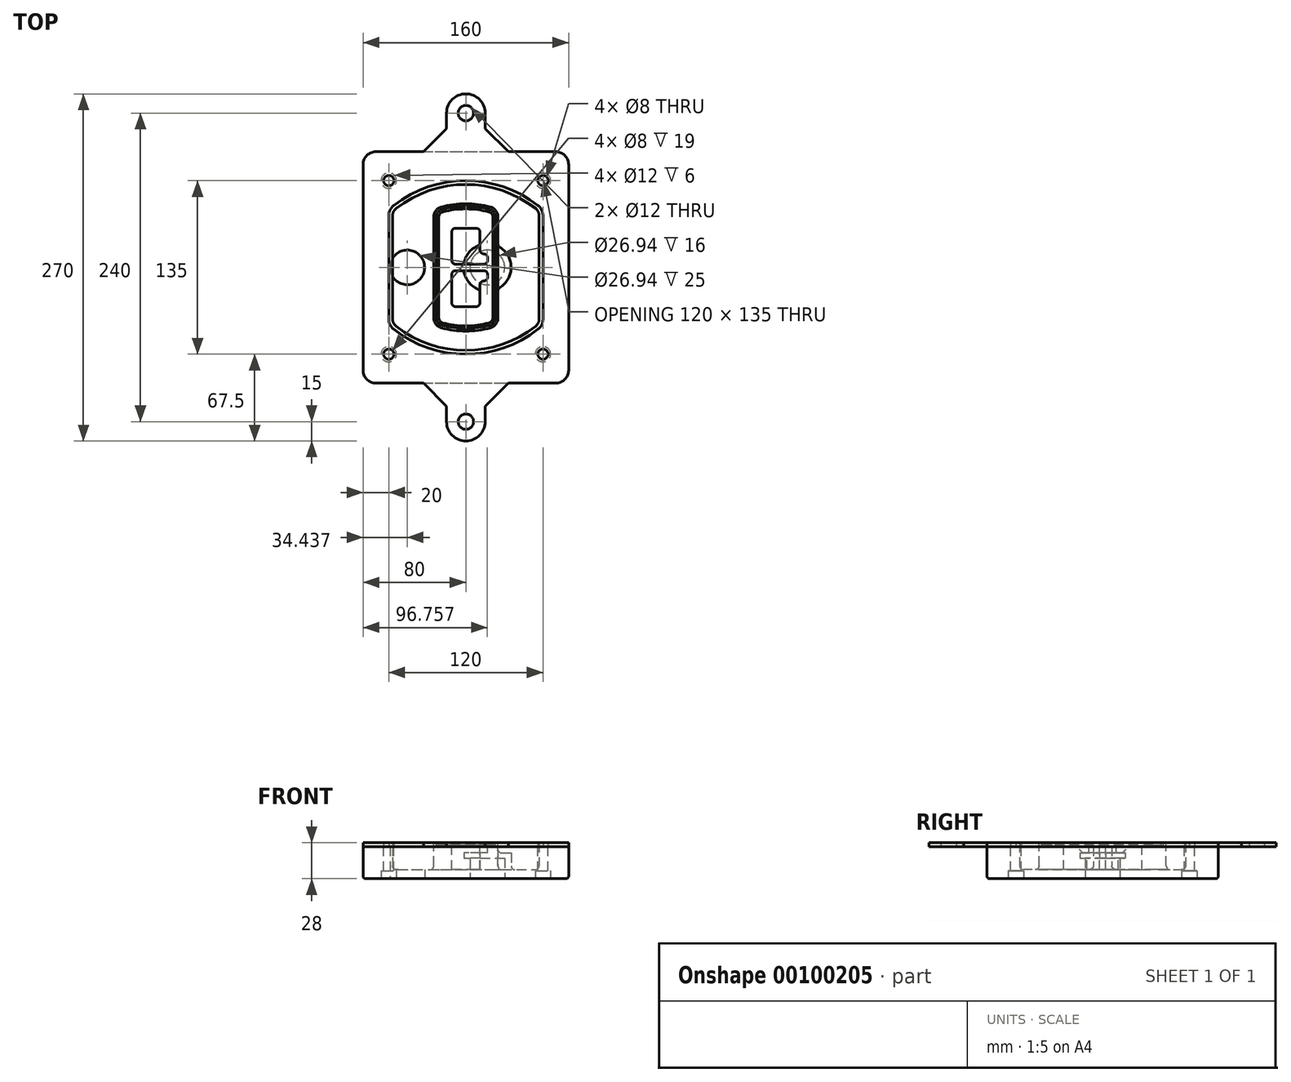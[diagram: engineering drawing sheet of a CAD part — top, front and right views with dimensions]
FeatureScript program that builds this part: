
annotation { "Feature Type Name" : "Feature", "Feature Type Description" : "" }
export const myFeature = defineFeature(function(context is Context, id is Id, definition is map)
    precondition{}
    {
        {
            var Q0;
            Q0=qCreatedBy(makeId("Top.planeOp"),FACE);
            var sketch = newSketch(context, id + "F0", { "sketchPlane" : qUnion([Q0])});
            skPoint(sketch, "E0.rect.middle", {"position": v(0, 0) * mm});
            skLineSegment(sketch, "E1.bottom", {"start": v(-70, -90) * mm, "end": v(70, -90) * mm});
            skLineSegment(sketch, "E1.top", {"start": v(-70, 90) * mm, "end": v(70, 90) * mm});
            skLineSegment(sketch, "E1.left", {"start": v(-80, -80) * mm, "end": v(-80, 80) * mm});
            skLineSegment(sketch, "E1.right", {"start": v(80, -80) * mm, "end": v(80, 80) * mm});
            skLineSegment(sketch, "E2", {"start": v(-80, 90) * mm, "end": v(80, -90) * mm, "construction": true});
            skLineSegment(sketch, "E3", {"start": v(80, 90) * mm, "end": v(-80, -90) * mm, "construction": true});
            skCircle(sketch, "E4", {"center": v(-60, 67.5) * mm, "radius": 4 * mm});
            skCircle(sketch, "E5", {"center": v(60, 67.5) * mm, "radius": 4 * mm});
            skCircle(sketch, "E6", {"center": v(60, -67.5) * mm, "radius": 4 * mm});
            skCircle(sketch, "E7", {"center": v(-60, -67.5) * mm, "radius": 4 * mm});
            skLineSegment(sketch, "E8", {"start": v(-60, 67.5) * mm, "end": v(60, 67.5) * mm, "construction": true});
            skLineSegment(sketch, "E9", {"start": v(60, 67.5) * mm, "end": v(60, -67.5) * mm, "construction": true});
            skLineSegment(sketch, "E10", {"start": v(60, -67.5) * mm, "end": v(-60, -67.5) * mm, "construction": true});
            skLineSegment(sketch, "E11", {"start": v(-60, -67.5) * mm, "end": v(-60, 67.5) * mm, "construction": true});
            skLineSegment(sketch, "E12", {"start": v(-60, 40.3) * mm, "end": v(-60, -40.3) * mm});
            skLineSegment(sketch, "E13", {"start": v(60, 40.3) * mm, "end": v(60, -40.3) * mm});
            skArc(sketch, "E14", {"start": v(56.15, 48.18) * mm, "mid": v(0, 67.5) * mm, "end": v(-56.15, 48.18) * mm});
            skArc(sketch, "E15", {"start": v(-56.15, -48.18) * mm, "mid": v(0, -67.5) * mm, "end": v(56.15, -48.18) * mm});
            skLineSegment(sketch, "E16", {"start": v(-60, 0) * mm, "end": v(60, 0) * mm, "construction": true});
            skPoint(sketch, "E17.visualSharp", {"position": v(-60, -45) * mm});
            skArc(sketch, "E17.filletArc", {"start": v(-60, -40.3) * mm, "mid": v(-58.99, -44.68) * mm, "end": v(-56.15, -48.18) * mm});
            skPoint(sketch, "E18.visualSharp", {"position": v(-60, 45) * mm});
            skArc(sketch, "E18.filletArc", {"start": v(-56.15, 48.18) * mm, "mid": v(-58.99, 44.68) * mm, "end": v(-60, 40.3) * mm});
            skPoint(sketch, "E19.visualSharp", {"position": v(60, 45) * mm});
            skArc(sketch, "E19.filletArc", {"start": v(60, 40.3) * mm, "mid": v(58.99, 44.68) * mm, "end": v(56.15, 48.18) * mm});
            skPoint(sketch, "E20.visualSharp", {"position": v(60, -45) * mm});
            skArc(sketch, "E20.filletArc", {"start": v(56.15, -48.18) * mm, "mid": v(58.99, -44.68) * mm, "end": v(60, -40.3) * mm});
            skPoint(sketch, "E21.visualSharp", {"position": v(-80, 90) * mm});
            skArc(sketch, "E21.filletArc", {"start": v(-70, 90) * mm, "mid": v(-77.07, 87.07) * mm, "end": v(-80, 80) * mm});
            skPoint(sketch, "E22.visualSharp", {"position": v(80, 90) * mm});
            skArc(sketch, "E22.filletArc", {"start": v(80, 80) * mm, "mid": v(77.07, 87.07) * mm, "end": v(70, 90) * mm});
            skPoint(sketch, "E23.visualSharp", {"position": v(80, -90) * mm});
            skArc(sketch, "E23.filletArc", {"start": v(70, -90) * mm, "mid": v(77.07, -87.07) * mm, "end": v(80, -80) * mm});
            skPoint(sketch, "E24.visualSharp", {"position": v(-80, -90) * mm});
            skArc(sketch, "E24.filletArc", {"start": v(-80, -80) * mm, "mid": v(-77.07, -87.07) * mm, "end": v(-70, -90) * mm});
            skArc(sketch, "E25.0", {"start": v(57, 40.3) * mm, "mid": v(56.3, 43.36) * mm, "end": v(54.3, 45.81) * mm});
            skLineSegment(sketch, "E25.1", {"start": v(57, 40.3) * mm, "end": v(57, -40.3) * mm});
            skArc(sketch, "E25.2", {"start": v(54.3, -45.81) * mm, "mid": v(56.3, -43.36) * mm, "end": v(57, -40.3) * mm});
            skArc(sketch, "E25.3", {"start": v(-54.3, -45.81) * mm, "mid": v(0, -64.5) * mm, "end": v(54.3, -45.81) * mm});
            skArc(sketch, "E25.4", {"start": v(-57, -40.3) * mm, "mid": v(-56.3, -43.36) * mm, "end": v(-54.3, -45.81) * mm});
            skArc(sketch, "E25.5", {"start": v(54.3, 45.81) * mm, "mid": v(0, 64.5) * mm, "end": v(-54.3, 45.81) * mm});
            skLineSegment(sketch, "E25.6", {"start": v(-57, 40.3) * mm, "end": v(-57, -40.3) * mm});
            skArc(sketch, "E25.7", {"start": v(-54.3, 45.81) * mm, "mid": v(-56.3, 43.36) * mm, "end": v(-57, 40.3) * mm});
            skArc(sketch, "E26.0", {"start": v(-58.62, 51.33) * mm, "mid": v(-62.58, 46.43) * mm, "end": v(-64, 40.3) * mm});
            skArc(sketch, "E26.1", {"start": v(58.62, 51.33) * mm, "mid": v(0, 71.5) * mm, "end": v(-58.62, 51.33) * mm});
            skArc(sketch, "E26.2", {"start": v(64, 40.3) * mm, "mid": v(62.58, 46.43) * mm, "end": v(58.62, 51.33) * mm});
            skLineSegment(sketch, "E26.3", {"start": v(64, 40.3) * mm, "end": v(64, -40.3) * mm});
            skArc(sketch, "E26.4", {"start": v(58.62, -51.33) * mm, "mid": v(62.58, -46.43) * mm, "end": v(64, -40.3) * mm});
            skLineSegment(sketch, "E26.5", {"start": v(-64, 40.3) * mm, "end": v(-64, -40.3) * mm});
            skArc(sketch, "E26.6", {"start": v(-58.62, -51.33) * mm, "mid": v(0, -71.5) * mm, "end": v(58.62, -51.33) * mm});
            skArc(sketch, "E26.7", {"start": v(-64, -40.3) * mm, "mid": v(-62.58, -46.43) * mm, "end": v(-58.62, -51.33) * mm});
            skSolve(sketch);
        }
        {
            var Q0;
            Q0=makeQuery(id+"F0.imprint","IMPRINT",FACE,{"disambiguationData":[TD([[makeQuery(id+"F0.imprint","IMPRINT",EDGE,{"derivedFrom":sQuery(id+"F0.wireOp",EDGE,"E1.bottom")}),1.0]])]});
            var Q1;
            Q1=makeQuery(id+"F0.imprint","IMPRINT",FACE,{"disambiguationData":[TD([[makeQuery(id+"F0.imprint","IMPRINT",EDGE,{"derivedFrom":sQuery(id+"F0.wireOp",EDGE,"E12")}),1.0]])]});
            var Q2;
            Q2=makeQuery(id+"F0.imprint","IMPRINT",FACE,{"disambiguationData":[TD([[makeQuery(id+"F0.imprint","IMPRINT",EDGE,{"derivedFrom":sQuery(id+"F0.wireOp",EDGE,"E25.0")}),1.0]])]});
            var Q3;
            Q3=makeQuery(id+"F0.imprint","IMPRINT",FACE,{"disambiguationData":[TD([[makeQuery(id+"F0.imprint","IMPRINT",EDGE,{"derivedFrom":sQuery(id+"F0.wireOp",EDGE,"E12")}),-1.0]])]});
            extrude(context, id + "F1", {"entities" : qUnion([Q0, Q1, Q2, Q3]), "oppositeDirection" : true, "depth" : 25 * mm});
        }
        {
            var Q0;
            Q0=makeQuery(id+"F0.imprint","IMPRINT",FACE,{"disambiguationData":[TD([[makeQuery(id+"F0.imprint","IMPRINT",EDGE,{"derivedFrom":sQuery(id+"F0.wireOp",EDGE,"E12")}),1.0]])]});
            extrude(context, id + "F2", {"entities" : qUnion([Q0]), "operationType" : NewBodyOperationType.ADD, "depth" : 3 * mm});
        }
        {
            var Q0;
            Q0=makeQuery(id+"F0.imprint","IMPRINT",FACE,{"disambiguationData":[TD([[makeQuery(id+"F0.imprint","IMPRINT",EDGE,{"derivedFrom":sQuery(id+"F0.wireOp",EDGE,"E25.0")}),1.0]])]});
            extrude(context, id + "F3", {"entities" : qUnion([Q0]), "operationType" : NewBodyOperationType.REMOVE, "oppositeDirection" : true, "depth" : 18 * mm});
        }
        {
            var Q0;
            Q0=makeQuery(id+"F2.opExtrude","CAP_FACE",FACE,{"disambiguationData":[OSD([sQuery(id+"F0.wireOp",EDGE,"E12"),sQuery(id+"F0.wireOp",EDGE,"E13"),sQuery(id+"F0.wireOp",EDGE,"E14"),sQuery(id+"F0.wireOp",EDGE,"E15"),sQuery(id+"F0.wireOp",EDGE,"E17.filletArc"),sQuery(id+"F0.wireOp",EDGE,"E18.filletArc"),sQuery(id+"F0.wireOp",EDGE,"E19.filletArc"),sQuery(id+"F0.wireOp",EDGE,"E20.filletArc"),sQuery(id+"F0.wireOp",EDGE,"E25.0"),sQuery(id+"F0.wireOp",EDGE,"E25.1"),sQuery(id+"F0.wireOp",EDGE,"E25.2"),sQuery(id+"F0.wireOp",EDGE,"E25.3"),sQuery(id+"F0.wireOp",EDGE,"E25.4"),sQuery(id+"F0.wireOp",EDGE,"E25.5"),sQuery(id+"F0.wireOp",EDGE,"E25.6"),sQuery(id+"F0.wireOp",EDGE,"E25.7")])],"isStart":false});
            var sketch = newSketch(context, id + "F4", { "sketchPlane" : qUnion([Q0])});
            skArc(sketch, "E27.0", {"start": v(-19.08, -46.97) * mm, "mid": v(0, -49.5) * mm, "end": v(19.08, -46.97) * mm});
            skArc(sketch, "E28.0", {"start": v(19.08, 46.97) * mm, "mid": v(0, 49.5) * mm, "end": v(-19.08, 46.97) * mm});
            skLineSegment(sketch, "E29", {"start": v(-25, 39.25) * mm, "end": v(-25, -39.25) * mm});
            skLineSegment(sketch, "E30", {"start": v(25, 39.25) * mm, "end": v(25, -39.25) * mm});
            skLineSegment(sketch, "E31", {"start": v(-25, 45.1) * mm, "end": v(25, 45.1) * mm, "construction": true});
            skLineSegment(sketch, "E32", {"start": v(-25, -45.1) * mm, "end": v(25, -45.1) * mm, "construction": true});
            skPoint(sketch, "E33.visualSharp", {"position": v(-25, 45.1) * mm});
            skArc(sketch, "E33.filletArc", {"start": v(-19.08, 46.97) * mm, "mid": v(-23.35, 44.11) * mm, "end": v(-25, 39.25) * mm});
            skPoint(sketch, "E34.visualSharp", {"position": v(25, 45.1) * mm});
            skArc(sketch, "E34.filletArc", {"start": v(25, 39.25) * mm, "mid": v(23.35, 44.11) * mm, "end": v(19.08, 46.97) * mm});
            skPoint(sketch, "E35.visualSharp", {"position": v(25, -45.1) * mm});
            skArc(sketch, "E35.filletArc", {"start": v(19.08, -46.97) * mm, "mid": v(23.35, -44.11) * mm, "end": v(25, -39.25) * mm});
            skPoint(sketch, "E36.visualSharp", {"position": v(-25, -45.1) * mm});
            skArc(sketch, "E36.filletArc", {"start": v(-25, -39.25) * mm, "mid": v(-23.35, -44.11) * mm, "end": v(-19.08, -46.97) * mm});
            skArc(sketch, "E37.0", {"start": v(54.3, 45.81) * mm, "mid": v(0, 64.5) * mm, "end": v(-54.3, 45.81) * mm});
            skArc(sketch, "E37.1", {"start": v(-54.3, 45.81) * mm, "mid": v(-56.3, 43.36) * mm, "end": v(-57, 40.3) * mm});
            skLineSegment(sketch, "E37.2", {"start": v(-57, 40.3) * mm, "end": v(-57, -40.3) * mm});
            skArc(sketch, "E37.3", {"start": v(-57, -40.3) * mm, "mid": v(-56.3, -43.36) * mm, "end": v(-54.3, -45.81) * mm});
            skArc(sketch, "E37.4", {"start": v(-54.3, -45.81) * mm, "mid": v(0, -64.5) * mm, "end": v(54.3, -45.81) * mm});
            skArc(sketch, "E37.5", {"start": v(54.3, -45.81) * mm, "mid": v(56.3, -43.36) * mm, "end": v(57, -40.3) * mm});
            skLineSegment(sketch, "E37.6", {"start": v(57, 40.3) * mm, "end": v(57, -40.3) * mm});
            skArc(sketch, "E37.7", {"start": v(57, 40.3) * mm, "mid": v(56.3, 43.36) * mm, "end": v(54.3, 45.81) * mm});
            skLineSegment(sketch, "E38.0", {"start": v(23, 39.25) * mm, "end": v(23, -39.25) * mm});
            skArc(sketch, "E38.1", {"start": v(18.56, -45.04) * mm, "mid": v(21.76, -42.9) * mm, "end": v(23, -39.25) * mm});
            skArc(sketch, "E38.2", {"start": v(-18.56, -45.04) * mm, "mid": v(0, -47.5) * mm, "end": v(18.56, -45.04) * mm});
            skArc(sketch, "E38.3", {"start": v(-23, -39.25) * mm, "mid": v(-21.76, -42.9) * mm, "end": v(-18.56, -45.04) * mm});
            skLineSegment(sketch, "E38.4", {"start": v(-23, 39.25) * mm, "end": v(-23, -39.25) * mm});
            skArc(sketch, "E38.5", {"start": v(23, 39.25) * mm, "mid": v(21.76, 42.9) * mm, "end": v(18.56, 45.04) * mm});
            skArc(sketch, "E38.6", {"start": v(-18.56, 45.04) * mm, "mid": v(-21.76, 42.9) * mm, "end": v(-23, 39.25) * mm});
            skArc(sketch, "E38.7", {"start": v(18.56, 45.04) * mm, "mid": v(0, 47.5) * mm, "end": v(-18.56, 45.04) * mm});
            skArc(sketch, "E39.0", {"start": v(21, 39.25) * mm, "mid": v(20.18, 41.68) * mm, "end": v(18.04, 43.1) * mm});
            skLineSegment(sketch, "E39.1", {"start": v(21, 39.25) * mm, "end": v(21, -39.25) * mm});
            skArc(sketch, "E39.2", {"start": v(18.04, -43.1) * mm, "mid": v(20.18, -41.68) * mm, "end": v(21, -39.25) * mm});
            skArc(sketch, "E39.3", {"start": v(-18.04, -43.1) * mm, "mid": v(0, -45.5) * mm, "end": v(18.04, -43.1) * mm});
            skArc(sketch, "E39.4", {"start": v(-21, -39.25) * mm, "mid": v(-20.18, -41.68) * mm, "end": v(-18.04, -43.1) * mm});
            skArc(sketch, "E39.5", {"start": v(18.04, 43.1) * mm, "mid": v(0, 45.5) * mm, "end": v(-18.04, 43.1) * mm});
            skLineSegment(sketch, "E39.6", {"start": v(-21, 39.25) * mm, "end": v(-21, -39.25) * mm});
            skArc(sketch, "E39.7", {"start": v(-18.04, 43.1) * mm, "mid": v(-20.18, 41.68) * mm, "end": v(-21, 39.25) * mm});
            skLineSegment(sketch, "E40", {"start": v(-25, 0) * mm, "end": v(25, 0) * mm, "construction": true});
            skLineSegment(sketch, "E41", {"start": v(-11, 5.5) * mm, "end": v(-11, 27.5) * mm});
            skLineSegment(sketch, "E42", {"start": v(-8, 30.5) * mm, "end": v(8, 30.5) * mm});
            skLineSegment(sketch, "E43", {"start": v(11, 27.5) * mm, "end": v(11, 13.5) * mm});
            skLineSegment(sketch, "E44", {"start": v(14, 10.5) * mm, "end": v(14, 10.5) * mm});
            skLineSegment(sketch, "E45", {"start": v(17, 7.5) * mm, "end": v(17, 5.5) * mm});
            skLineSegment(sketch, "E46", {"start": v(14, 2.5) * mm, "end": v(-8, 2.5) * mm});
            skPoint(sketch, "E47.visualSharp", {"position": v(-11, 30.5) * mm});
            skArc(sketch, "E47.filletArc", {"start": v(-8, 30.5) * mm, "mid": v(-10.12, 29.62) * mm, "end": v(-11, 27.5) * mm});
            skPoint(sketch, "E48.visualSharp", {"position": v(11, 30.5) * mm});
            skArc(sketch, "E48.filletArc", {"start": v(11, 27.5) * mm, "mid": v(10.12, 29.62) * mm, "end": v(8, 30.5) * mm});
            skPoint(sketch, "E49.visualSharp", {"position": v(11, 10.5) * mm});
            skArc(sketch, "E49.filletArc", {"start": v(11, 13.5) * mm, "mid": v(11.88, 11.38) * mm, "end": v(14, 10.5) * mm});
            skPoint(sketch, "E50.visualSharp", {"position": v(17, 10.5) * mm});
            skArc(sketch, "E50.filletArc", {"start": v(17, 7.5) * mm, "mid": v(16.12, 9.62) * mm, "end": v(14, 10.5) * mm});
            skPoint(sketch, "E51.visualSharp", {"position": v(17, 2.5) * mm});
            skArc(sketch, "E51.filletArc", {"start": v(14, 2.5) * mm, "mid": v(16.12, 3.38) * mm, "end": v(17, 5.5) * mm});
            skPoint(sketch, "E52.visualSharp", {"position": v(-11, 2.5) * mm});
            skArc(sketch, "E52.filletArc", {"start": v(-11, 5.5) * mm, "mid": v(-10.12, 3.38) * mm, "end": v(-8, 2.5) * mm});
            skLineSegment(sketch, "E53.0.MirrorCS", {"start": v(14, -2.5) * mm, "end": v(-8, -2.5) * mm});
            skArc(sketch, "E54.0.MirrorCS", {"start": v(-11, -5.5) * mm, "mid": v(-10.12, -3.38) * mm, "end": v(-8, -2.5) * mm});
            skLineSegment(sketch, "E55.0.MirrorCS", {"start": v(-11, -5.5) * mm, "end": v(-11, -27.5) * mm});
            skArc(sketch, "E56.0.MirrorCS", {"start": v(-8, -30.5) * mm, "mid": v(-10.12, -29.62) * mm, "end": v(-11, -27.5) * mm});
            skLineSegment(sketch, "E57.0.MirrorCS", {"start": v(-8, -30.5) * mm, "end": v(8, -30.5) * mm});
            skArc(sketch, "E58.0.MirrorCS", {"start": v(11, -27.5) * mm, "mid": v(10.12, -29.62) * mm, "end": v(8, -30.5) * mm});
            skLineSegment(sketch, "E59.0.MirrorCS", {"start": v(11, -27.5) * mm, "end": v(11, -13.5) * mm});
            skArc(sketch, "E60.0.MirrorCS", {"start": v(11, -13.5) * mm, "mid": v(11.88, -11.38) * mm, "end": v(14, -10.5) * mm});
            skArc(sketch, "E61.0.MirrorCS", {"start": v(17, -7.5) * mm, "mid": v(16.12, -9.62) * mm, "end": v(14, -10.5) * mm});
            skLineSegment(sketch, "E62.0.MirrorCS", {"start": v(17, -7.5) * mm, "end": v(17, -5.5) * mm});
            skArc(sketch, "E63.0.MirrorCS", {"start": v(14, -2.5) * mm, "mid": v(16.12, -3.38) * mm, "end": v(17, -5.5) * mm});
            skSolve(sketch);
        }
        {
            var Q0;
            Q0=makeQuery(id+"F4.imprint","IMPRINT",FACE,{"disambiguationData":[TD([[makeQuery(id+"F4.imprint","IMPRINT",EDGE,{"derivedFrom":sQuery(id+"F4.wireOp",EDGE,"E27.0")}),1.0]])]});
            var Q1;
            Q1=makeQuery(id+"F4.imprint","IMPRINT",FACE,{"disambiguationData":[TD([[makeQuery(id+"F4.imprint","IMPRINT",EDGE,{"derivedFrom":sQuery(id+"F4.wireOp",EDGE,"E38.0")}),-1.0]])]});
            var Q2;
            Q2=makeQuery(id+"F4.imprint","IMPRINT",FACE,{"disambiguationData":[TD([[makeQuery(id+"F4.imprint","IMPRINT",EDGE,{"derivedFrom":sQuery(id+"F4.wireOp",EDGE,"E39.0")}),1.0]])]});
            extrude(context, id + "F5", {"entities" : qUnion([Q0, Q1, Q2]), "operationType" : NewBodyOperationType.ADD, "endBound" : BoundingType.UP_TO_NEXT, "oppositeDirection" : true, "depth" : 25 * mm});
        }
        {
            var Q0;
            Q0=makeQuery(id+"F4.imprint","IMPRINT",FACE,{"disambiguationData":[TD([[makeQuery(id+"F4.imprint","IMPRINT",EDGE,{"derivedFrom":sQuery(id+"F4.wireOp",EDGE,"E38.0")}),-1.0]])]});
            extrude(context, id + "F6", {"entities" : qUnion([Q0]), "operationType" : NewBodyOperationType.REMOVE, "oppositeDirection" : true, "depth" : 2 * mm});
        }
        {
            var Q0;
            Q0=makeQuery(id+"F1.opExtrude","CAP_FACE",FACE,{"disambiguationData":[OSD([sQuery(id+"F0.wireOp",EDGE,"E1.bottom"),sQuery(id+"F0.wireOp",EDGE,"E1.top"),sQuery(id+"F0.wireOp",EDGE,"E1.left"),sQuery(id+"F0.wireOp",EDGE,"E1.right"),sQuery(id+"F0.wireOp",EDGE,"E4"),sQuery(id+"F0.wireOp",EDGE,"E5"),sQuery(id+"F0.wireOp",EDGE,"E6"),sQuery(id+"F0.wireOp",EDGE,"E7"),sQuery(id+"F0.wireOp",EDGE,"E21.filletArc"),sQuery(id+"F0.wireOp",EDGE,"E22.filletArc"),sQuery(id+"F0.wireOp",EDGE,"E23.filletArc"),sQuery(id+"F0.wireOp",EDGE,"E24.filletArc")])],"isStart":false});
            var sketch = newSketch(context, id + "F7", { "sketchPlane" : qUnion([Q0])});
            skCircle(sketch, "E64", {"center": v(16.76, 0) * mm, "radius": 13.47 * mm});
            skCircle(sketch, "E65", {"center": v(-45.56, 0) * mm, "radius": 13.47 * mm});
            skLineSegment(sketch, "E66", {"start": v(80, 0) * mm, "end": v(-80, 0) * mm});
            skCircle(sketch, "E67", {"center": v(16.76, 0) * mm, "radius": 18.47 * mm});
            skCircle(sketch, "E68", {"center": v(60, -67.5) * mm, "radius": 6 * mm});
            skCircle(sketch, "E69", {"center": v(-60, -67.5) * mm, "radius": 6 * mm});
            skCircle(sketch, "E70", {"center": v(-60, 67.5) * mm, "radius": 6 * mm});
            skCircle(sketch, "E71", {"center": v(60, 67.5) * mm, "radius": 6 * mm});
            skSolve(sketch);
        }
        {
            var Q0;
            {var subQ1=sQuery(id+"F7.wireOp",EDGE,"E66");var subQ4=sQuery(id+"F7.wireOp",EDGE,"E64");var subQ6=makeQuery(id+"F7.imprint","INTERSECT",VERTEX,{"disambiguationData":[OD(0.0)],"derivedFrom":[subQ4,subQ1]});Q0=makeQuery(id+"F7.imprint","IMPRINT",FACE,{"disambiguationData":[TD([[makeQuery(id+"F7.imprint","IMPRINT",EDGE,{"disambiguationData":[TD([[subQ6,-1.0]])],"derivedFrom":subQ4}),-1.0]])]});}
            var Q1;
            {var subQ0=sQuery(id+"F7.wireOp",EDGE,"E66");var subQ1=sQuery(id+"F7.wireOp",EDGE,"E64");var subQ3=makeQuery(id+"F7.imprint","INTERSECT",VERTEX,{"disambiguationData":[OD(0.0)],"derivedFrom":[subQ1,subQ0]});Q1=makeQuery(id+"F7.imprint","IMPRINT",FACE,{"disambiguationData":[TD([[makeQuery(id+"F7.imprint","IMPRINT",EDGE,{"disambiguationData":[TD([[subQ3,-1.0]])],"derivedFrom":subQ1}),1.0]])]});}
            var Q2;
            {var subQ0=sQuery(id+"F7.wireOp",EDGE,"E66");var subQ1=sQuery(id+"F7.wireOp",EDGE,"E64");var subQ3=makeQuery(id+"F7.imprint","INTERSECT",VERTEX,{"disambiguationData":[OD(0.0)],"derivedFrom":[subQ1,subQ0]});Q2=makeQuery(id+"F7.imprint","IMPRINT",FACE,{"disambiguationData":[TD([[makeQuery(id+"F7.imprint","IMPRINT",EDGE,{"disambiguationData":[TD([[subQ3,1.0]])],"derivedFrom":subQ1}),1.0]])]});}
            var Q3;
            {var subQ1=sQuery(id+"F7.wireOp",EDGE,"E66");var subQ4=sQuery(id+"F7.wireOp",EDGE,"E64");var subQ6=makeQuery(id+"F7.imprint","INTERSECT",VERTEX,{"disambiguationData":[OD(0.0)],"derivedFrom":[subQ4,subQ1]});Q3=makeQuery(id+"F7.imprint","IMPRINT",FACE,{"disambiguationData":[TD([[makeQuery(id+"F7.imprint","IMPRINT",EDGE,{"disambiguationData":[TD([[subQ6,1.0]])],"derivedFrom":subQ4}),-1.0]])]});}
            extrude(context, id + "F8", {"entities" : qUnion([Q0, Q1, Q2, Q3]), "operationType" : NewBodyOperationType.ADD, "oppositeDirection" : true, "depth" : 20 * mm});
        }
        {
            var Q0;
            {var subQ0=sQuery(id+"F7.wireOp",EDGE,"E66");var subQ1=sQuery(id+"F7.wireOp",EDGE,"E64");var subQ3=makeQuery(id+"F7.imprint","INTERSECT",VERTEX,{"disambiguationData":[OD(0.0)],"derivedFrom":[subQ1,subQ0]});Q0=makeQuery(id+"F7.imprint","IMPRINT",FACE,{"disambiguationData":[TD([[makeQuery(id+"F7.imprint","IMPRINT",EDGE,{"disambiguationData":[TD([[subQ3,-1.0]])],"derivedFrom":subQ1}),1.0]])]});}
            var Q1;
            {var subQ0=sQuery(id+"F7.wireOp",EDGE,"E66");var subQ1=sQuery(id+"F7.wireOp",EDGE,"E64");var subQ3=makeQuery(id+"F7.imprint","INTERSECT",VERTEX,{"disambiguationData":[OD(0.0)],"derivedFrom":[subQ1,subQ0]});Q1=makeQuery(id+"F7.imprint","IMPRINT",FACE,{"disambiguationData":[TD([[makeQuery(id+"F7.imprint","IMPRINT",EDGE,{"disambiguationData":[TD([[subQ3,1.0]])],"derivedFrom":subQ1}),1.0]])]});}
            extrude(context, id + "F9", {"entities" : qUnion([Q0, Q1]), "operationType" : NewBodyOperationType.REMOVE, "oppositeDirection" : true, "depth" : 16 * mm});
        }
        {
            var Q0;
            {var subQ0=sQuery(id+"F7.wireOp",EDGE,"E66");var subQ1=sQuery(id+"F7.wireOp",EDGE,"E65");var subQ3=makeQuery(id+"F7.imprint","INTERSECT",VERTEX,{"disambiguationData":[OD(0.0)],"derivedFrom":[subQ1,subQ0]});Q0=makeQuery(id+"F7.imprint","IMPRINT",FACE,{"disambiguationData":[TD([[makeQuery(id+"F7.imprint","IMPRINT",EDGE,{"disambiguationData":[TD([[subQ3,-1.0]])],"derivedFrom":subQ1}),1.0]])]});}
            var Q1;
            {var subQ0=sQuery(id+"F7.wireOp",EDGE,"E66");var subQ1=sQuery(id+"F7.wireOp",EDGE,"E65");var subQ3=makeQuery(id+"F7.imprint","INTERSECT",VERTEX,{"disambiguationData":[OD(0.0)],"derivedFrom":[subQ1,subQ0]});Q1=makeQuery(id+"F7.imprint","IMPRINT",FACE,{"disambiguationData":[TD([[makeQuery(id+"F7.imprint","IMPRINT",EDGE,{"disambiguationData":[TD([[subQ3,1.0]])],"derivedFrom":subQ1}),1.0]])]});}
            extrude(context, id + "F10", {"entities" : qUnion([Q0, Q1]), "operationType" : NewBodyOperationType.REMOVE, "oppositeDirection" : true, "depth" : 25 * mm});
        }
        {
            var Q0;
            Q0=makeQuery(id+"F7.imprint","IMPRINT",FACE,{"disambiguationData":[TD([[makeQuery(id+"F7.imprint","IMPRINT",EDGE,{"derivedFrom":sQuery(id+"F7.wireOp",EDGE,"E68")}),1.0]])]});
            var Q1;
            Q1=makeQuery(id+"F7.imprint","IMPRINT",FACE,{"disambiguationData":[TD([[makeQuery(id+"F7.imprint","IMPRINT",EDGE,{"derivedFrom":makeQuery(id+"F1.opExtrude","CAP_EDGE",EDGE,{"disambiguationData":[OSD([sQuery(id+"F0.wireOp",EDGE,"E5")])],"isStart":false})}),-1.0]])]});
            var Q2;
            Q2=makeQuery(id+"F7.imprint","IMPRINT",FACE,{"disambiguationData":[TD([[makeQuery(id+"F7.imprint","IMPRINT",EDGE,{"derivedFrom":sQuery(id+"F7.wireOp",EDGE,"E69")}),1.0]])]});
            var Q3;
            Q3=makeQuery(id+"F7.imprint","IMPRINT",FACE,{"disambiguationData":[TD([[makeQuery(id+"F7.imprint","IMPRINT",EDGE,{"derivedFrom":makeQuery(id+"F1.opExtrude","CAP_EDGE",EDGE,{"disambiguationData":[OSD([sQuery(id+"F0.wireOp",EDGE,"E4")])],"isStart":false})}),-1.0]])]});
            var Q4;
            Q4=makeQuery(id+"F7.imprint","IMPRINT",FACE,{"disambiguationData":[TD([[makeQuery(id+"F7.imprint","IMPRINT",EDGE,{"derivedFrom":sQuery(id+"F7.wireOp",EDGE,"E70")}),1.0]])]});
            var Q5;
            Q5=makeQuery(id+"F7.imprint","IMPRINT",FACE,{"disambiguationData":[TD([[makeQuery(id+"F7.imprint","IMPRINT",EDGE,{"derivedFrom":makeQuery(id+"F1.opExtrude","CAP_EDGE",EDGE,{"disambiguationData":[OSD([sQuery(id+"F0.wireOp",EDGE,"E7")])],"isStart":false})}),-1.0]])]});
            var Q6;
            Q6=makeQuery(id+"F7.imprint","IMPRINT",FACE,{"disambiguationData":[TD([[makeQuery(id+"F7.imprint","IMPRINT",EDGE,{"derivedFrom":sQuery(id+"F7.wireOp",EDGE,"E71")}),1.0]])]});
            var Q7;
            Q7=makeQuery(id+"F7.imprint","IMPRINT",FACE,{"disambiguationData":[TD([[makeQuery(id+"F7.imprint","IMPRINT",EDGE,{"derivedFrom":makeQuery(id+"F1.opExtrude","CAP_EDGE",EDGE,{"disambiguationData":[OSD([sQuery(id+"F0.wireOp",EDGE,"E6")])],"isStart":false})}),-1.0]])]});
            extrude(context, id + "F11", {"entities" : qUnion([Q0, Q1, Q2, Q3, Q4, Q5, Q6, Q7]), "operationType" : NewBodyOperationType.REMOVE, "oppositeDirection" : true, "depth" : 6 * mm});
        }
        {
            var Q0;
            Q0=makeQuery(id+"F9.boolean.opBoolean","COPY",FACE,{"derivedFrom":makeQuery(id+"F9.opExtrude","CAP_FACE",FACE,{"disambiguationData":[OSD([sQuery(id+"F7.wireOp",EDGE,"E64")])],"isStart":false})});
            var sketch = newSketch(context, id + "F12", { "sketchPlane" : qUnion([Q0])});
            skArc(sketch, "E72.0", {"start": v(11, 17.55) * mm, "mid": v(2.57, 11.82) * mm, "end": v(-1.54, 2.5) * mm});
            skArc(sketch, "E72.1", {"start": v(-1.54, -2.5) * mm, "mid": v(2.57, -11.82) * mm, "end": v(11, -17.55) * mm});
            skLineSegment(sketch, "E73", {"start": v(-1.54, -2.5) * mm, "end": v(14, -2.5) * mm});
            skLineSegment(sketch, "E74.0", {"start": v(14, 2.5) * mm, "end": v(-1.54, 2.5) * mm});
            skArc(sketch, "E74.1", {"start": v(14, 2.5) * mm, "mid": v(16.12, 3.38) * mm, "end": v(17, 5.5) * mm});
            skLineSegment(sketch, "E74.2", {"start": v(17, 7.5) * mm, "end": v(17, 5.5) * mm});
            skArc(sketch, "E74.3", {"start": v(17, 7.5) * mm, "mid": v(16.12, 9.62) * mm, "end": v(14, 10.5) * mm});
            skArc(sketch, "E74.4", {"start": v(11, 13.5) * mm, "mid": v(11.88, 11.38) * mm, "end": v(14, 10.5) * mm});
            skLineSegment(sketch, "E74.5", {"start": v(11, 17.55) * mm, "end": v(11, 13.5) * mm});
            skLineSegment(sketch, "E74.7", {"start": v(14, -2.5) * mm, "end": v(-1.54, -2.5) * mm});
            skArc(sketch, "E74.8", {"start": v(14, -2.5) * mm, "mid": v(16.12, -3.38) * mm, "end": v(17, -5.5) * mm});
            skLineSegment(sketch, "E74.9", {"start": v(17, -7.5) * mm, "end": v(17, -5.5) * mm});
            skArc(sketch, "E74.10", {"start": v(17, -7.5) * mm, "mid": v(16.12, -9.62) * mm, "end": v(14, -10.5) * mm});
            skArc(sketch, "E74.11", {"start": v(11, -13.5) * mm, "mid": v(11.88, -11.38) * mm, "end": v(14, -10.5) * mm});
            skLineSegment(sketch, "E74.12", {"start": v(11, -17.55) * mm, "end": v(11, -13.5) * mm});
            skPoint(sketch, "E75.orphan", {"position": v(11, -27.5) * mm});
            skPoint(sketch, "E76.orphan", {"position": v(-8, -2.5) * mm});
            skPoint(sketch, "E77.orphan", {"position": v(-8, 2.5) * mm});
            skPoint(sketch, "E78.orphan", {"position": v(11, 27.5) * mm});
            skSolve(sketch);
        }
        {
            var Q0;
            {var subQ7=sQuery(id+"F12.wireOp",EDGE,"E72.0");var subQ14=sQuery(id+"F12.wireOp",EDGE,"E72.1");var subQ16=sQuery(id+"F12.wireOp",EDGE,"E74.1");var subQ18=sQuery(id+"F12.wireOp",EDGE,"E74.8");Q0=qUnion([makeQuery(id+"F12.imprint","IMPRINT",FACE,{"disambiguationData":[TD([[makeQuery(id+"F12.imprint","IMPRINT",EDGE,{"derivedFrom":subQ7}),1.0]])]}),makeQuery(id+"F12.imprint","IMPRINT",FACE,{"disambiguationData":[TD([[makeQuery(id+"F12.imprint","IMPRINT",EDGE,{"derivedFrom":subQ14}),1.0]])]}),makeQuery(id+"F12.imprint","IMPRINT",FACE,{"disambiguationData":[TD([[makeQuery(id+"F12.imprint","IMPRINT",EDGE,{"derivedFrom":subQ16}),1.0]])]}),makeQuery(id+"F12.imprint","IMPRINT",FACE,{"disambiguationData":[TD([[makeQuery(id+"F12.imprint","IMPRINT",EDGE,{"derivedFrom":subQ18}),-1.0]])]})]);}
            var Q1;
            Q1=makeQuery(id+"F5.boolean.opBoolean","SPLIT",FACE,{"disambiguationData":[TD([makeQuery(id+"F5.opExtrude","SWEPT_FACE",FACE,{"disambiguationData":[OSD([sQuery(id+"F4.wireOp",EDGE,"E41")])]})])],"derivedFrom":makeQuery(id+"F3.boolean.opBoolean","COPY",FACE,{"derivedFrom":makeQuery(id+"F3.opExtrude","CAP_FACE",FACE,{"disambiguationData":[OSD([sQuery(id+"F0.wireOp",EDGE,"E25.0"),sQuery(id+"F0.wireOp",EDGE,"E25.1"),sQuery(id+"F0.wireOp",EDGE,"E25.2"),sQuery(id+"F0.wireOp",EDGE,"E25.3"),sQuery(id+"F0.wireOp",EDGE,"E25.4"),sQuery(id+"F0.wireOp",EDGE,"E25.5"),sQuery(id+"F0.wireOp",EDGE,"E25.6"),sQuery(id+"F0.wireOp",EDGE,"E25.7")])],"isStart":false})})});
            extrude(context, id + "F13", {"entities" : qUnion([Q0]), "operationType" : NewBodyOperationType.REMOVE, "endBound" : BoundingType.UP_TO_SURFACE, "endBoundEntityFace" : qUnion([Q1]), "depth" : 25 * mm});
        }
        {
            var Q0;
            Q0=makeQuery(id+"F3.boolean.opBoolean","COPY",EDGE,{"derivedFrom":makeQuery(id+"F3.opExtrude","CAP_EDGE",EDGE,{"disambiguationData":[OSD([sQuery(id+"F0.wireOp",EDGE,"E25.6")])],"isStart":false})});
            var Q1;
            Q1=makeQuery(id+"F8.boolean.opBoolean","INTERSECT",EDGE,{"derivedFrom":[makeQuery(id+"F5.opExtrude","SWEPT_FACE",FACE,{"disambiguationData":[OSD([sQuery(id+"F4.wireOp",EDGE,"E30")])]}),makeQuery(id+"F8.opExtrude","CAP_FACE",FACE,{"disambiguationData":[OSD([sQuery(id+"F7.wireOp",EDGE,"E67")])],"isStart":false})]});
            var Q2;
            Q2=makeQuery(id+"F8.boolean.opBoolean","INTERSECT",EDGE,{"disambiguationData":[OD(1.0)],"derivedFrom":[makeQuery(id+"F5.opExtrude","SWEPT_FACE",FACE,{"disambiguationData":[OSD([sQuery(id+"F4.wireOp",EDGE,"E30")])]}),makeQuery(id+"F8.opExtrude","SWEPT_FACE",FACE,{"disambiguationData":[OSD([sQuery(id+"F7.wireOp",EDGE,"E67")])]})]});
            var Q3;
            {var subQ0=sQuery(id+"F4.wireOp",EDGE,"E30");Q3=makeQuery(id+"F8.boolean.opBoolean","SPLIT",EDGE,{"disambiguationData":[TD([makeQuery(id+"F5.opExtrude","SWEPT_FACE",FACE,{"disambiguationData":[OSD([sQuery(id+"F4.wireOp",EDGE,"E35.filletArc")])]})])],"derivedFrom":makeQuery(id+"F5.opExtrude","CAP_EDGE",EDGE,{"disambiguationData":[OSD([subQ0])],"isStart":false})});}
            var Q4;
            {var subQ0=sQuery(id+"F0.wireOp",EDGE,"E25.7");var subQ1=sQuery(id+"F0.wireOp",EDGE,"E25.1");var subQ2=sQuery(id+"F0.wireOp",EDGE,"E25.6");var subQ3=sQuery(id+"F0.wireOp",EDGE,"E25.5");var subQ4=sQuery(id+"F0.wireOp",EDGE,"E25.4");var subQ5=sQuery(id+"F0.wireOp",EDGE,"E25.0");var subQ6=sQuery(id+"F0.wireOp",EDGE,"E25.2");var subQ7=sQuery(id+"F0.wireOp",EDGE,"E25.3");Q4=makeQuery(id+"F8.boolean.opBoolean","INTERSECT",EDGE,{"derivedFrom":[makeQuery(id+"F5.boolean.opBoolean","SPLIT",FACE,{"disambiguationData":[TD([makeQuery(id+"F2.opExtrude","SWEPT_FACE",FACE,{"disambiguationData":[OSD([subQ5])]})])],"derivedFrom":makeQuery(id+"F3.boolean.opBoolean","COPY",FACE,{"derivedFrom":makeQuery(id+"F3.opExtrude","CAP_FACE",FACE,{"disambiguationData":[OSD([subQ5,subQ1,subQ6,subQ7,subQ4,subQ3,subQ2,subQ0])],"isStart":false})})}),makeQuery(id+"F8.opExtrude","SWEPT_FACE",FACE,{"disambiguationData":[OSD([sQuery(id+"F7.wireOp",EDGE,"E67")])]})]});}
            var Q5;
            Q5=makeQuery(id+"F8.boolean.opBoolean","INTERSECT",EDGE,{"disambiguationData":[OD(0.0)],"derivedFrom":[makeQuery(id+"F5.opExtrude","SWEPT_FACE",FACE,{"disambiguationData":[OSD([sQuery(id+"F4.wireOp",EDGE,"E30")])]}),makeQuery(id+"F8.opExtrude","SWEPT_FACE",FACE,{"disambiguationData":[OSD([sQuery(id+"F7.wireOp",EDGE,"E67")])]})]});
            fillet(context, id + "F14", {"entities" : qUnion([Q0, Q1, Q2, Q3, Q4, Q5]), "radius" : 3 * mm, "tangentPropagation" : true, "allowEdgeOverflow" : false});
        }
        {
            var Q0;
            Q0=makeQuery(id+"F1.opExtrude","CAP_EDGE",EDGE,{"disambiguationData":[OSD([sQuery(id+"F0.wireOp",EDGE,"E1.bottom")])],"isStart":false});
            fillet(context, id + "F15", {"entities" : qUnion([Q0]), "radius" : 2 * mm, "tangentPropagation" : true, "allowEdgeOverflow" : false});
        }
        {
            var Q0;
            {var subQ0=sQuery(id+"F0.wireOp",EDGE,"E22.filletArc");var subQ1=sQuery(id+"F0.wireOp",EDGE,"E7");var subQ2=sQuery(id+"F0.wireOp",EDGE,"E6");var subQ3=sQuery(id+"F0.wireOp",EDGE,"E5");var subQ4=sQuery(id+"F0.wireOp",EDGE,"E4");var subQ5=sQuery(id+"F0.wireOp",EDGE,"E1.bottom");var subQ6=sQuery(id+"F0.wireOp",EDGE,"E21.filletArc");var subQ7=sQuery(id+"F0.wireOp",EDGE,"E1.top");var subQ8=sQuery(id+"F0.wireOp",EDGE,"E1.left");var subQ9=sQuery(id+"F0.wireOp",EDGE,"E1.right");var subQ10=sQuery(id+"F0.wireOp",EDGE,"E23.filletArc");var subQ11=sQuery(id+"F0.wireOp",EDGE,"E24.filletArc");Q0=makeQuery(id+"F2.boolean.opBoolean","SPLIT",FACE,{"disambiguationData":[TD([makeQuery(id+"F1.opExtrude","SWEPT_FACE",FACE,{"disambiguationData":[OSD([subQ5])]})])],"derivedFrom":makeQuery(id+"F1.opExtrude","CAP_FACE",FACE,{"disambiguationData":[OSD([subQ5,subQ7,subQ8,subQ9,subQ4,subQ3,subQ2,subQ1,subQ6,subQ0,subQ10,subQ11])],"isStart":true})});}
            var sketch = newSketch(context, id + "F16", { "sketchPlane" : qUnion([Q0])});
            skLineSegment(sketch, "E79", {"start": v(-33, 90) * mm, "end": v(-15, 108) * mm});
            skLineSegment(sketch, "E80", {"start": v(-15, 108) * mm, "end": v(-15, 120) * mm});
            skLineSegment(sketch, "E81", {"start": v(15, 120) * mm, "end": v(15, 108) * mm});
            skLineSegment(sketch, "E82", {"start": v(15, 108) * mm, "end": v(33, 90) * mm});
            skArc(sketch, "E83", {"start": v(15, 120) * mm, "mid": v(0, 135) * mm, "end": v(-15, 120) * mm});
            skCircle(sketch, "E84", {"center": v(0, 120) * mm, "radius": 6 * mm});
            skLineSegment(sketch, "E85.MirrorCS", {"start": v(-15, -108) * mm, "end": v(-15, -120) * mm});
            skArc(sketch, "E86.MirrorCS", {"start": v(15, -120) * mm, "mid": v(0, -135) * mm, "end": v(-15, -120) * mm});
            skCircle(sketch, "E87.MirrorC", {"center": v(0, -120) * mm, "radius": 6 * mm});
            skLineSegment(sketch, "E88.MirrorCS", {"start": v(15, -120) * mm, "end": v(15, -108) * mm});
            skLineSegment(sketch, "E89.MirrorCS", {"start": v(-33, -90) * mm, "end": v(-15, -108) * mm});
            skLineSegment(sketch, "E90.MirrorCS", {"start": v(15, -108) * mm, "end": v(33, -90) * mm});
            skCircle(sketch, "E91.0", {"center": v(-60, 67.5) * mm, "radius": 4 * mm});
            skLineSegment(sketch, "E91.1", {"start": v(-70, 90) * mm, "end": v(70, 90) * mm});
            skArc(sketch, "E91.2", {"start": v(-70, 90) * mm, "mid": v(-77.07, 87.07) * mm, "end": v(-80, 80) * mm});
            skLineSegment(sketch, "E91.3", {"start": v(-80, -80) * mm, "end": v(-80, 80) * mm});
            skArc(sketch, "E91.4", {"start": v(80, 80) * mm, "mid": v(77.07, 87.07) * mm, "end": v(70, 90) * mm});
            skLineSegment(sketch, "E91.5", {"start": v(80, -80) * mm, "end": v(80, 80) * mm});
            skCircle(sketch, "E91.6", {"center": v(60, 67.5) * mm, "radius": 4 * mm});
            skArc(sketch, "E91.7", {"start": v(-80, -80) * mm, "mid": v(-77.07, -87.07) * mm, "end": v(-70, -90) * mm});
            skLineSegment(sketch, "E91.8", {"start": v(-70, -90) * mm, "end": v(70, -90) * mm});
            skArc(sketch, "E91.9", {"start": v(70, -90) * mm, "mid": v(77.07, -87.07) * mm, "end": v(80, -80) * mm});
            skCircle(sketch, "E91.10", {"center": v(60, -67.5) * mm, "radius": 4 * mm});
            skLineSegment(sketch, "E91.11", {"start": v(-60, 40.3) * mm, "end": v(-60, -40.3) * mm});
            skArc(sketch, "E91.12", {"start": v(-56.15, 48.18) * mm, "mid": v(-58.99, 44.68) * mm, "end": v(-60, 40.3) * mm});
            skArc(sketch, "E91.13", {"start": v(56.15, 48.18) * mm, "mid": v(0, 67.5) * mm, "end": v(-56.15, 48.18) * mm});
            skArc(sketch, "E91.14", {"start": v(60, 40.3) * mm, "mid": v(58.99, 44.68) * mm, "end": v(56.15, 48.18) * mm});
            skLineSegment(sketch, "E91.15", {"start": v(60, 40.3) * mm, "end": v(60, -40.3) * mm});
            skArc(sketch, "E91.16", {"start": v(56.15, -48.18) * mm, "mid": v(58.99, -44.68) * mm, "end": v(60, -40.3) * mm});
            skArc(sketch, "E91.17", {"start": v(-56.15, -48.18) * mm, "mid": v(0, -67.5) * mm, "end": v(56.15, -48.18) * mm});
            skArc(sketch, "E91.18", {"start": v(-60, -40.3) * mm, "mid": v(-58.99, -44.68) * mm, "end": v(-56.15, -48.18) * mm});
            skCircle(sketch, "E91.19", {"center": v(-60, -67.5) * mm, "radius": 4 * mm});
            skSolve(sketch);
        }
        {
            var Q0;
            {var subQ1=sQuery(id+"F16.wireOp",EDGE,"E79");Q0=makeQuery(id+"F16.imprint","IMPRINT",FACE,{"disambiguationData":[TD([[makeQuery(id+"F16.imprint","IMPRINT",EDGE,{"derivedFrom":subQ1}),-1.0]])]});}
            var Q1;
            Q1=makeQuery(id+"F16.imprint","IMPRINT",FACE,{"disambiguationData":[TD([[makeQuery(id+"F16.imprint","IMPRINT",EDGE,{"derivedFrom":sQuery(id+"F16.wireOp",EDGE,"E91.0")}),-1.0]])]});
            var Q2;
            Q2=makeQuery(id+"F16.imprint","IMPRINT",FACE,{"disambiguationData":[TD([[makeQuery(id+"F16.imprint","IMPRINT",EDGE,{"derivedFrom":sQuery(id+"F16.wireOp",EDGE,"E85.MirrorCS")}),1.0]])]});
            var Q3;
            Q3=makeQuery(id+"F2.opExtrude","CAP_FACE",FACE,{"disambiguationData":[OSD([sQuery(id+"F0.wireOp",EDGE,"E12"),sQuery(id+"F0.wireOp",EDGE,"E13"),sQuery(id+"F0.wireOp",EDGE,"E14"),sQuery(id+"F0.wireOp",EDGE,"E15"),sQuery(id+"F0.wireOp",EDGE,"E17.filletArc"),sQuery(id+"F0.wireOp",EDGE,"E18.filletArc"),sQuery(id+"F0.wireOp",EDGE,"E19.filletArc"),sQuery(id+"F0.wireOp",EDGE,"E20.filletArc"),sQuery(id+"F0.wireOp",EDGE,"E25.0"),sQuery(id+"F0.wireOp",EDGE,"E25.1"),sQuery(id+"F0.wireOp",EDGE,"E25.2"),sQuery(id+"F0.wireOp",EDGE,"E25.3"),sQuery(id+"F0.wireOp",EDGE,"E25.4"),sQuery(id+"F0.wireOp",EDGE,"E25.5"),sQuery(id+"F0.wireOp",EDGE,"E25.6"),sQuery(id+"F0.wireOp",EDGE,"E25.7")])],"isStart":false});
            extrude(context, id + "F17", {"entities" : qUnion([Q0, Q1, Q2]), "endBound" : BoundingType.UP_TO_SURFACE, "endBoundEntityFace" : qUnion([Q3]), "depth" : 25 * mm});
        }
    });
